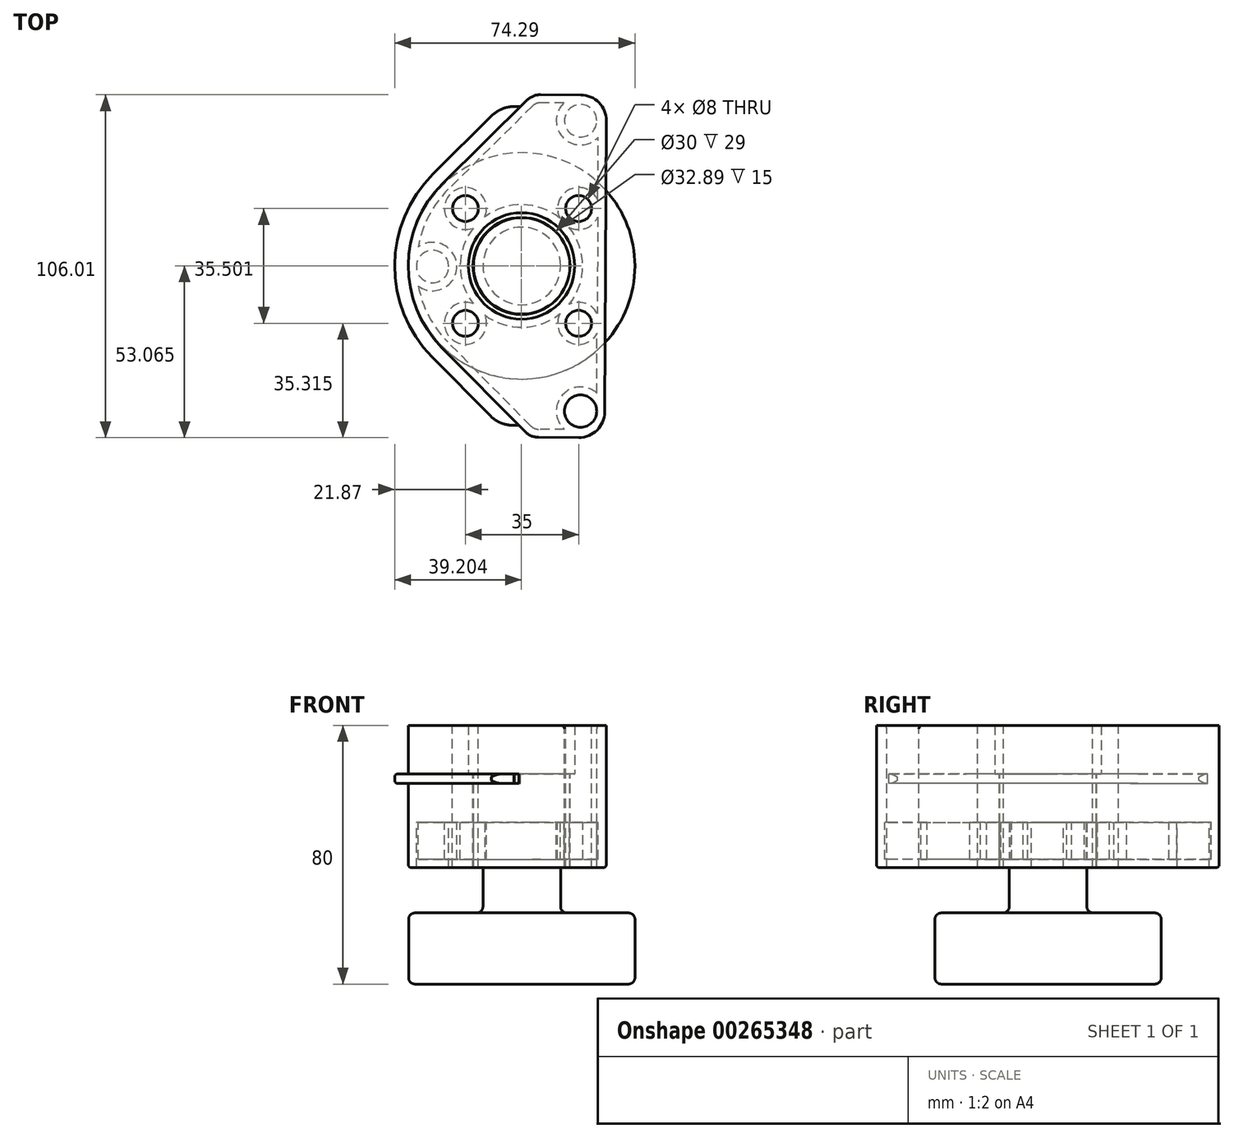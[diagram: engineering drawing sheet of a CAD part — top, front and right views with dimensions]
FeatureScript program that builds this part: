
annotation { "Feature Type Name" : "Feature", "Feature Type Description" : "" }
export const myFeature = defineFeature(function(context is Context, id is Id, definition is map)
    precondition{}
    {
        {
            var Q0;
            Q0=qCreatedBy(makeId("Top.planeOp"),FACE);
            var sketch = newSketch(context, id + "F0", { "sketchPlane" : qUnion([Q0])});
            skLineSegment(sketch, "E0", {"start": v(12.96, -51.64) * mm, "end": v(25.4, -51.71) * mm});
            skLineSegment(sketch, "E1", {"start": v(-16.96, -23.88) * mm, "end": v(8.74, -49.87) * mm});
            skLineSegment(sketch, "E2.MirrorCS", {"start": v(-16.69, 26.87) * mm, "end": v(7.36, 50.65) * mm});
            skLineSegment(sketch, "E3.MirrorCS", {"start": v(13.54, 54.3) * mm, "end": v(25.98, 54.23) * mm});
            skLineSegment(sketch, "E4", {"start": v(33.9, 46.22) * mm, "end": v(33.42, -43.78) * mm});
            skPoint(sketch, "E5.visualSharp", {"position": v(-42.34, 1.16) * mm});
            skArc(sketch, "E5.filletArc", {"start": v(-16.69, 26.87) * mm, "mid": v(-27.34, 1.55) * mm, "end": v(-16.96, -23.88) * mm});
            skPoint(sketch, "E6.visualSharp", {"position": v(33.37, -51.75) * mm});
            skArc(sketch, "E6.filletArc", {"start": v(25.4, -51.71) * mm, "mid": v(31.05, -49.4) * mm, "end": v(33.42, -43.78) * mm});
            skPoint(sketch, "E7.visualSharp", {"position": v(33.95, 54.2) * mm});
            skArc(sketch, "E7.filletArc", {"start": v(33.9, 46.22) * mm, "mid": v(31.6, 51.87) * mm, "end": v(25.98, 54.23) * mm});
            skPoint(sketch, "E8.visualSharp", {"position": v(10.49, -51.63) * mm});
            skArc(sketch, "E8.filletArc", {"start": v(8.74, -49.87) * mm, "mid": v(10.68, -51.18) * mm, "end": v(12.96, -51.64) * mm});
            skPoint(sketch, "E9.visualSharp", {"position": v(11.06, 54.32) * mm});
            skArc(sketch, "E9.filletArc", {"start": v(13.54, 54.3) * mm, "mid": v(11.25, 53.86) * mm, "end": v(9.3, 52.57) * mm});
            skLineSegment(sketch, "E10.0", {"start": v(5.3, -47.91) * mm, "end": v(6.82, -47.92) * mm});
            skArc(sketch, "E10.1", {"start": v(-1.73, -45.26) * mm, "mid": v(1.53, -47.28) * mm, "end": v(5.3, -47.91) * mm});
            skLineSegment(sketch, "E10.2", {"start": v(-19.95, -26.83) * mm, "end": v(-1.73, -45.26) * mm});
            skLineSegment(sketch, "E10.3", {"start": v(5.85, 50.66) * mm, "end": v(7.36, 50.65) * mm});
            skArc(sketch, "E10.4", {"start": v(5.85, 50.66) * mm, "mid": v(2.06, 50.06) * mm, "end": v(-1.22, 48.07) * mm});
            skLineSegment(sketch, "E10.5", {"start": v(-19.64, 29.85) * mm, "end": v(-1.22, 48.07) * mm});
            skArc(sketch, "E10.6", {"start": v(-19.64, 29.85) * mm, "mid": v(-31.54, 1.57) * mm, "end": v(-19.95, -26.83) * mm});
            skLineSegment(sketch, "E11", {"start": v(7.36, 50.65) * mm, "end": v(9.3, 52.57) * mm});
            skCircle(sketch, "E12", {"center": v(7.66, 1.36) * mm, "radius": 15 * mm});
            skCircle(sketch, "E13.0", {"center": v(7.66, 1.36) * mm, "radius": 16.45 * mm});
            skCircle(sketch, "E14", {"center": v(25.94, 46.26) * mm, "radius": 5 * mm});
            skCircle(sketch, "E15", {"center": v(25.33, 19.1) * mm, "radius": 4 * mm});
            skCircle(sketch, "E16", {"center": v(-9.67, 19.1) * mm, "radius": 4 * mm});
            skLineSegment(sketch, "E17", {"start": v(7.66, 1.36) * mm, "end": v(8.55, 1.36) * mm});
            skCircle(sketch, "E18.MirrorC", {"center": v(25.33, -16.4) * mm, "radius": 4 * mm});
            skCircle(sketch, "E19.MirrorC", {"center": v(-9.67, -16.4) * mm, "radius": 4 * mm});
            skCircle(sketch, "E20.MirrorC", {"center": v(25.94, -43.55) * mm, "radius": 5 * mm});
            skCircle(sketch, "E21", {"center": v(-19.84, 1.16) * mm, "radius": 5 * mm});
            skPoint(sketch, "E21.centerSnap0", {"position": v(-27.34, 1.55) * mm});
            skSolve(sketch);
        }
        {
            var Q0;
            Q0=makeQuery(id+"F0.imprint","IMPRINT",FACE,{"disambiguationData":[TD([[makeQuery(id+"F0.imprint","IMPRINT",EDGE,{"derivedFrom":sQuery(id+"F0.wireOp",EDGE,"E0")}),1.0]])]});
            extrude(context, id + "F1", {"entities" : qUnion([Q0]), "oppositeDirection" : true, "depth" : 29 * mm});
        }
        {
            var Q0;
            Q0=makeQuery(id+"F1.opExtrude","CAP_FACE",FACE,{"disambiguationData":[OSD([sQuery(id+"F0.wireOp",EDGE,"E0"),sQuery(id+"F0.wireOp",EDGE,"E1"),sQuery(id+"F0.wireOp",EDGE,"E2.MirrorCS"),sQuery(id+"F0.wireOp",EDGE,"E3.MirrorCS"),sQuery(id+"F0.wireOp",EDGE,"E4"),sQuery(id+"F0.wireOp",EDGE,"E5.filletArc"),sQuery(id+"F0.wireOp",EDGE,"E6.filletArc"),sQuery(id+"F0.wireOp",EDGE,"E7.filletArc"),sQuery(id+"F0.wireOp",EDGE,"E8.filletArc"),sQuery(id+"F0.wireOp",EDGE,"E9.filletArc"),sQuery(id+"F0.wireOp",EDGE,"E11"),sQuery(id+"F0.wireOp",EDGE,"E13.0")])],"isStart":true});
            shell(context, id + "F2", {"entities" : qUnion([Q0]), "thickness" : 2.5 * mm});
        }
        {
            var Q0;
            Q0=makeQuery(id+"F0.imprint","IMPRINT",FACE,{"disambiguationData":[TD([[makeQuery(id+"F0.imprint","IMPRINT",EDGE,{"derivedFrom":sQuery(id+"F0.wireOp",EDGE,"E2.MirrorCS")}),1.0]])]});
            extrude(context, id + "F3", {"entities" : qUnion([Q0]), "operationType" : NewBodyOperationType.ADD, "oppositeDirection" : true, "depth" : 3 * mm});
        }
        {
            var Q0;
            Q0=makeQuery(id+"F0.imprint","IMPRINT",FACE,{"disambiguationData":[TD([[makeQuery(id+"F0.imprint","IMPRINT",EDGE,{"derivedFrom":sQuery(id+"F0.wireOp",EDGE,"E14")}),1.0]])]});
            var Q1;
            Q1=makeQuery(id+"F0.imprint","IMPRINT",FACE,{"disambiguationData":[TD([[makeQuery(id+"F0.imprint","IMPRINT",EDGE,{"derivedFrom":sQuery(id+"F0.wireOp",EDGE,"E21")}),1.0]])]});
            var Q2;
            Q2=makeQuery(id+"F0.imprint","IMPRINT",FACE,{"disambiguationData":[TD([[makeQuery(id+"F0.imprint","IMPRINT",EDGE,{"derivedFrom":sQuery(id+"F0.wireOp",EDGE,"E20.MirrorC")}),-1.0]])]});
            var Q3;
            Q3=sQuery(id+"F0.wireOp",EDGE,"E14");
            var Q4;
            Q4=sQuery(id+"F0.wireOp",EDGE,"E21");
            var Q5;
            Q5=sQuery(id+"F0.wireOp",EDGE,"E20.MirrorC");
            extrude(context, id + "F4", {"entities" : qUnion([Q0, Q1, Q2]), "surfaceEntities" : qUnion([Q3, Q4, Q5]), "depth" : 30 * mm, "symmetric" : true});
        }
        {
            var Q0;
            Q0=makeQuery(id+"F0.imprint","IMPRINT",FACE,{"disambiguationData":[TD([[makeQuery(id+"F0.imprint","IMPRINT",EDGE,{"derivedFrom":sQuery(id+"F0.wireOp",EDGE,"E12")}),-1.0]])]});
            extrude(context, id + "F5", {"entities" : qUnion([Q0]), "operationType" : NewBodyOperationType.ADD, "oppositeDirection" : true, "depth" : 29 * mm});
        }
        {
            var Q0;
            Q0=sQuery(id+"F0.wireOp",EDGE,"E17");
            cPlane(context, id + "F6", {"entities" : qUnion([Q0]), "cplaneType" : CPlaneType.LINE_ANGLE, "offset" : 25 * mm, "angle" : 0 * degree, "width" : 150 * mm, "height" : 150 * mm});
        }
        {
            var Q0;
            Q0=qCreatedBy(id+"F6.planeOp",FACE);
            var sketch = newSketch(context, id + "F7", { "sketchPlane" : qUnion([Q0])});
            skLineSegment(sketch, "E22", {"start": v(-7.75, 0) * mm, "end": v(-7.75, -260.13) * mm});
            skLineSegment(sketch, "E23", {"start": v(-7.75, 0) * mm, "end": v(-22.65, 0) * mm});
            skLineSegment(sketch, "E24", {"start": v(-22.65, 0) * mm, "end": v(-22.65, -29) * mm});
            skLineSegment(sketch, "E25", {"start": v(-22.65, -29) * mm, "end": v(-19.75, -29) * mm});
            skLineSegment(sketch, "E26", {"start": v(-19.75, -29) * mm, "end": v(-19.75, -43) * mm});
            skLineSegment(sketch, "E27", {"start": v(-19.75, -43) * mm, "end": v(-42.75, -43) * mm});
            skLineSegment(sketch, "E28", {"start": v(-42.75, -43) * mm, "end": v(-42.75, -65) * mm});
            skLineSegment(sketch, "E29", {"start": v(-42.75, -65) * mm, "end": v(-7.75, -65) * mm});
            skSolve(sketch);
        }
        {
            var Q0;
            {var subQ1=sQuery(id+"F7.wireOp",EDGE,"E23");Q0=makeQuery(id+"F7.imprint","IMPRINT",FACE,{"disambiguationData":[TD([[makeQuery(id+"F7.imprint","IMPRINT",EDGE,{"derivedFrom":subQ1}),1.0]])]});}
            var Q1;
            Q1=sQuery(id+"F7.wireOp",EDGE,"E24");
            var Q2;
            Q2=sQuery(id+"F7.wireOp",EDGE,"E25");
            var Q3;
            Q3=sQuery(id+"F7.wireOp",EDGE,"E26");
            var Q4;
            Q4=sQuery(id+"F7.wireOp",EDGE,"E27");
            var Q5;
            Q5=sQuery(id+"F7.wireOp",EDGE,"E28");
            var Q6;
            Q6=sQuery(id+"F7.wireOp",EDGE,"E22");
            revolve(context, id + "F8", {"entities" : qUnion([Q0]), "surfaceEntities" : qUnion([Q1, Q2, Q3, Q4, Q5]), "axis" : qUnion([Q6]), "revolveType" : RevolveType.FULL});
        }
        {
            var Q0;
            Q0=makeQuery(id+"F8.opRevolve","SWEPT_EDGE",EDGE,{"disambiguationData":[OSD([sQuery(id+"F7.wireOp",EDGE,"E27"),sQuery(id+"F7.wireOp",EDGE,"E28")])]});
            var Q1;
            Q1=makeQuery(id+"F8.opRevolve","SWEPT_EDGE",EDGE,{"disambiguationData":[OSD([sQuery(id+"F7.wireOp",EDGE,"E26"),sQuery(id+"F7.wireOp",EDGE,"E27")])]});
            var Q2;
            Q2=makeQuery(id+"F8.opRevolve","SWEPT_EDGE",EDGE,{"disambiguationData":[OSD([sQuery(id+"F7.wireOp",EDGE,"E28"),sQuery(id+"F7.wireOp",EDGE,"E29")])]});
            fillet(context, id + "F9", {"entities" : qUnion([Q0, Q1, Q2]), "radius" : 2 * mm, "tangentPropagation" : true, "allowEdgeOverflow" : false});
        }
        {
            var Q0;
            Q0=makeQuery(id+"F1.opExtrude","CAP_EDGE",EDGE,{"disambiguationData":[OSD([sQuery(id+"F0.wireOp",EDGE,"E5.filletArc")])],"isStart":false});
            var Q1;
            Q1=makeQuery(id+"F3.opExtrude","CAP_EDGE",EDGE,{"disambiguationData":[OSD([sQuery(id+"F0.wireOp",EDGE,"E10.6")])],"isStart":true});
            var Q2;
            Q2=makeQuery(id+"F1.opExtrude","CAP_EDGE",EDGE,{"disambiguationData":[OSD([sQuery(id+"F0.wireOp",EDGE,"E7.filletArc")])],"isStart":true});
            var Q3;
            Q3=makeQuery(id+"F3.opExtrude","CAP_EDGE",EDGE,{"disambiguationData":[OSD([sQuery(id+"F0.wireOp",EDGE,"E10.6")])],"isStart":false});
            var Q4;
            Q4=makeQuery(id+"F4.opExtrude","CAP_EDGE",EDGE,{"disambiguationData":[OSD([sQuery(id+"F0.wireOp",EDGE,"E21")])],"isStart":false});
            var Q5;
            Q5=makeQuery(id+"F4.opExtrude","CAP_EDGE",EDGE,{"disambiguationData":[OSD([sQuery(id+"F0.wireOp",EDGE,"E14")])],"isStart":false});
            var Q6;
            Q6=makeQuery(id+"F4.opExtrude","CAP_EDGE",EDGE,{"disambiguationData":[OSD([sQuery(id+"F0.wireOp",EDGE,"E20.MirrorC")])],"isStart":false});
            fillet(context, id + "F10", {"entities" : qUnion([Q0, Q1, Q2, Q3, Q4, Q5, Q6]), "radius" : 1 * mm, "tangentPropagation" : true, "allowEdgeOverflow" : false});
        }
    });
